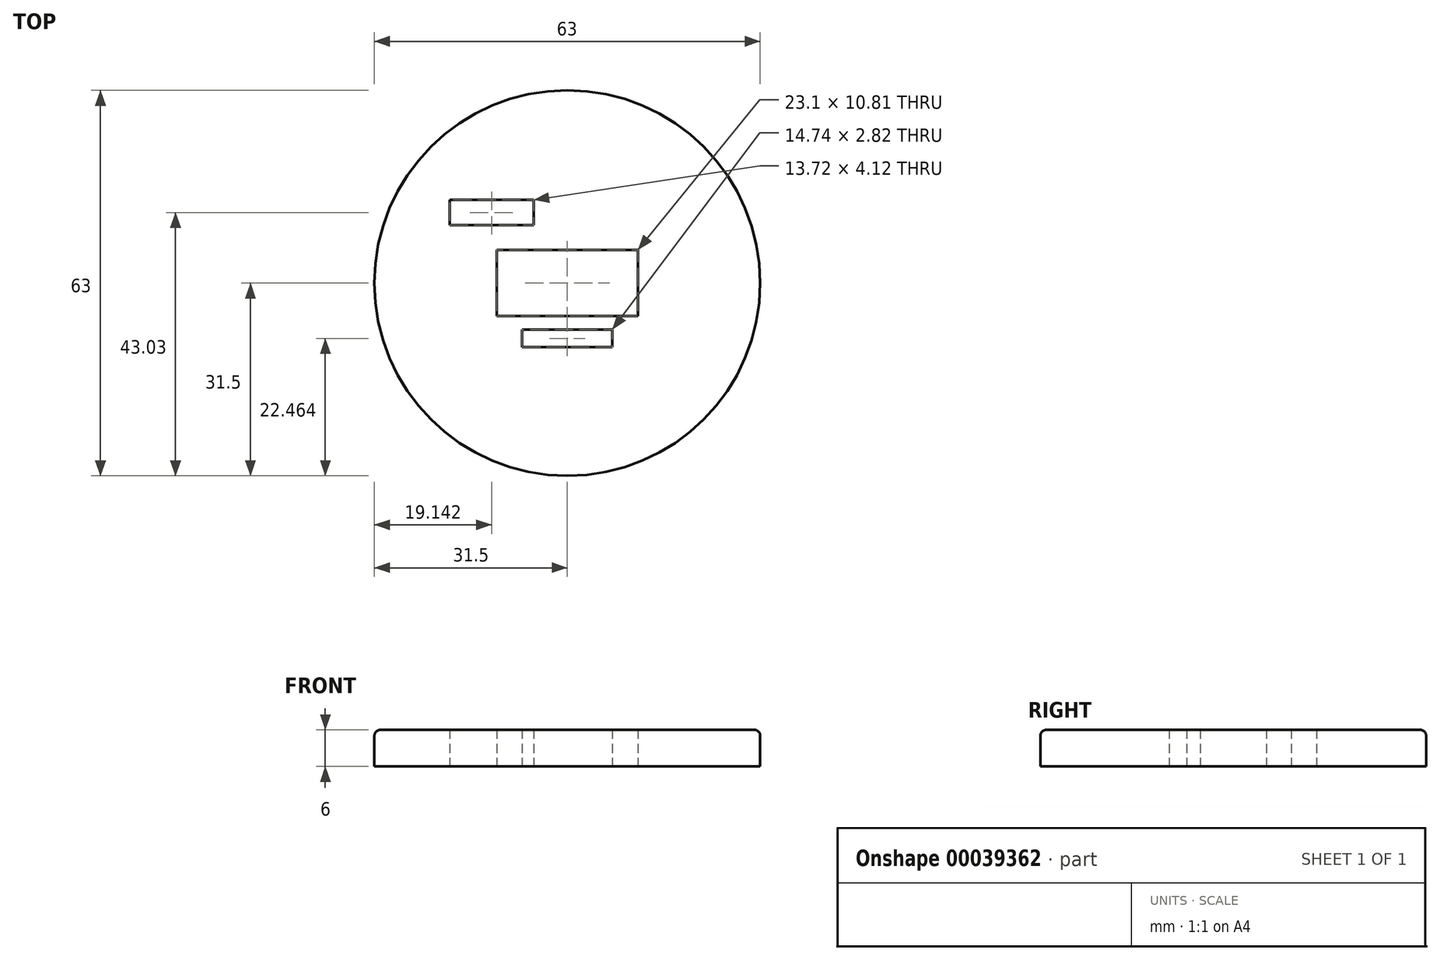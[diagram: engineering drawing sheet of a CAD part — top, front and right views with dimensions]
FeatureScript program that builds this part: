
annotation { "Feature Type Name" : "Feature", "Feature Type Description" : "" }
export const myFeature = defineFeature(function(context is Context, id is Id, definition is map)
    precondition{}
    {
        {
            var Q0;
            Q0=qCreatedBy(makeId("Top.planeOp"),FACE);
            var sketch = newSketch(context, id + "F0", { "sketchPlane" : qUnion([Q0])});
            skCircle(sketch, "E0", {"center": v(0, 0) * mm, "radius": 31.5 * mm});
            skCircle(sketch, "E1", {"center": v(0, 0) * mm, "radius": 3.5 * mm});
            skLineSegment(sketch, "E2.bottom", {"start": v(-19.22, 9.47) * mm, "end": v(-5.5, 9.47) * mm});
            skLineSegment(sketch, "E2.top", {"start": v(-19.22, 13.59) * mm, "end": v(-5.5, 13.59) * mm});
            skLineSegment(sketch, "E2.left", {"start": v(-19.22, 9.47) * mm, "end": v(-19.22, 13.59) * mm});
            skLineSegment(sketch, "E2.right", {"start": v(-5.5, 9.47) * mm, "end": v(-5.5, 13.59) * mm});
            skLineSegment(sketch, "E3.bottom", {"start": v(-11.55, 5.4) * mm, "end": v(11.55, 5.4) * mm});
            skLineSegment(sketch, "E3.top", {"start": v(-11.55, -5.4) * mm, "end": v(11.55, -5.4) * mm});
            skLineSegment(sketch, "E3.left", {"start": v(-11.55, 5.4) * mm, "end": v(-11.55, -5.4) * mm});
            skLineSegment(sketch, "E3.right", {"start": v(11.55, 5.4) * mm, "end": v(11.55, -5.4) * mm});
            skLineSegment(sketch, "E4.bottom", {"start": v(-7.37, -7.63) * mm, "end": v(7.37, -7.63) * mm});
            skLineSegment(sketch, "E4.top", {"start": v(-7.37, -10.44) * mm, "end": v(7.37, -10.44) * mm});
            skLineSegment(sketch, "E4.left", {"start": v(-7.37, -7.63) * mm, "end": v(-7.37, -10.44) * mm});
            skLineSegment(sketch, "E4.right", {"start": v(7.37, -7.63) * mm, "end": v(7.37, -10.44) * mm});
            skPoint(sketch, "E4.middle", {"position": v(0, -9.04) * mm});
            skSolve(sketch);
        }
        {
            var Q0;
            Q0=makeQuery(id+"F0.imprint","IMPRINT",FACE,{"disambiguationData":[TD([[makeQuery(id+"F0.imprint","IMPRINT",EDGE,{"derivedFrom":sQuery(id+"F0.wireOp",EDGE,"E0")}),1.0]])]});
            extrude(context, id + "F1", {"entities" : qUnion([Q0]), "depth" : 6 * mm});
        }
        {
            var Q0;
            Q0=makeQuery(id+"F1.opExtrude","CAP_EDGE",EDGE,{"disambiguationData":[OSD([sQuery(id+"F0.wireOp",EDGE,"E0")])],"isStart":false});
            fillet(context, id + "F2", {"entities" : qUnion([Q0]), "radius" : 1 * mm, "tangentPropagation" : true, "allowEdgeOverflow" : false});
        }
        {
            var Q0;
            Q0=makeQuery(id+"F1.opExtrude","CAP_FACE",FACE,{"disambiguationData":[OSD([sQuery(id+"F0.wireOp",EDGE,"E0"),sQuery(id+"F0.wireOp",EDGE,"E2.bottom"),sQuery(id+"F0.wireOp",EDGE,"E2.top"),sQuery(id+"F0.wireOp",EDGE,"E2.left"),sQuery(id+"F0.wireOp",EDGE,"E2.right"),sQuery(id+"F0.wireOp",EDGE,"E3.bottom"),sQuery(id+"F0.wireOp",EDGE,"E3.top"),sQuery(id+"F0.wireOp",EDGE,"E3.left"),sQuery(id+"F0.wireOp",EDGE,"E3.right"),sQuery(id+"F0.wireOp",EDGE,"E4.bottom"),sQuery(id+"F0.wireOp",EDGE,"E4.top"),sQuery(id+"F0.wireOp",EDGE,"E4.left"),sQuery(id+"F0.wireOp",EDGE,"E4.right")])],"isStart":false});
            var sketch = newSketch(context, id + "F3", { "sketchPlane" : qUnion([Q0])});
            skLineSegment(sketch, "E5.bottom", {"start": v(9.87, 14.63) * mm, "end": v(-3.41, 14.63) * mm});
            skLineSegment(sketch, "E5.top", {"start": v(9.87, 17.95) * mm, "end": v(-3.41, 17.95) * mm});
            skLineSegment(sketch, "E5.left", {"start": v(9.87, 14.63) * mm, "end": v(9.87, 17.95) * mm});
            skLineSegment(sketch, "E5.right", {"start": v(-3.41, 14.63) * mm, "end": v(-3.41, 17.95) * mm});
            skPoint(sketch, "E5.middle", {"position": v(3.23, 16.3) * mm});
            skLineSegment(sketch, "E6.bottom", {"start": v(-5, 8.91) * mm, "end": v(5, 8.91) * mm});
            skLineSegment(sketch, "E6.top", {"start": v(-5, -1.09) * mm, "end": v(5, -1.09) * mm});
            skLineSegment(sketch, "E6.left", {"start": v(-5, 8.91) * mm, "end": v(-5, -1.09) * mm});
            skLineSegment(sketch, "E6.right", {"start": v(5, 8.91) * mm, "end": v(5, -1.09) * mm});
            skPoint(sketch, "E6.middle", {"position": v(0, 3.91) * mm});
            skSolve(sketch);
        }
    });
